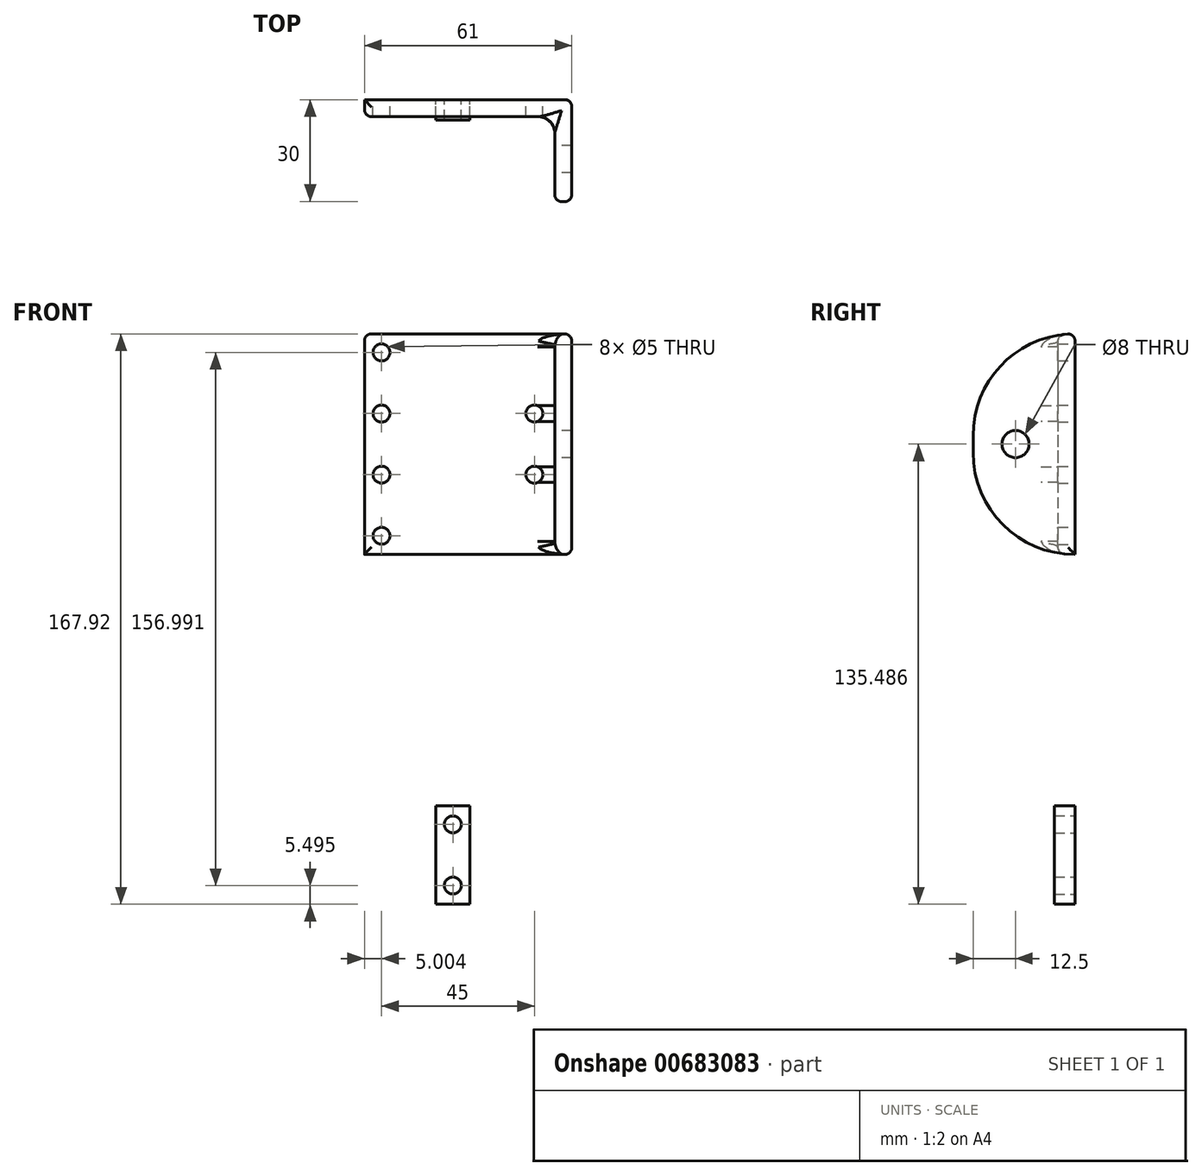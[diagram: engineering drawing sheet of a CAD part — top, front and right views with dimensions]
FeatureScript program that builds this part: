
annotation { "Feature Type Name" : "Feature", "Feature Type Description" : "" }
export const myFeature = defineFeature(function(context is Context, id is Id, definition is map)
    precondition{}
    {
        {
            var Q0;
            Q0=qCreatedBy(makeId("Front.planeOp"),FACE);
            var sketch = newSketch(context, id + "F0", { "sketchPlane" : qUnion([Q0])});
            skLineSegment(sketch, "E0.bottom", {"start": v(12.21, 1.73) * mm, "end": v(68.21, 1.73) * mm});
            skLineSegment(sketch, "E0.top", {"start": v(12.21, -63.27) * mm, "end": v(68.21, -63.27) * mm});
            skLineSegment(sketch, "E0.left", {"start": v(12.21, 1.73) * mm, "end": v(12.21, -63.27) * mm});
            skLineSegment(sketch, "E0.right", {"start": v(68.21, 1.73) * mm, "end": v(68.21, -63.27) * mm});
            skLineSegment(sketch, "E1", {"start": v(17.21, 42.37) * mm, "end": v(17.21, -87.97) * mm, "construction": true});
            skLineSegment(sketch, "E2", {"start": v(62.21, 27.17) * mm, "end": v(62.21, -88.73) * mm, "construction": true});
            skLineSegment(sketch, "E3", {"start": v(236.56, -57.77) * mm, "end": v(-18.05, -57.77) * mm, "construction": true});
            skLineSegment(sketch, "E4", {"start": v(95.96, -39.77) * mm, "end": v(-20.33, -39.77) * mm, "construction": true});
            skPoint(sketch, "E5", {"position": v(17.21, -57.77) * mm});
            skPoint(sketch, "E6", {"position": v(62.21, -39.77) * mm});
            skLineSegment(sketch, "E7.bottom", {"start": v(68.21, 1.73) * mm, "end": v(73.21, 1.73) * mm});
            skLineSegment(sketch, "E7.top", {"start": v(68.21, -63.27) * mm, "end": v(73.21, -63.27) * mm});
            skLineSegment(sketch, "E7.right", {"start": v(73.21, 1.73) * mm, "end": v(73.21, -63.27) * mm});
            skLineSegment(sketch, "E8", {"start": v(86.47, -3.77) * mm, "end": v(-13.74, -3.77) * mm, "construction": true});
            skLineSegment(sketch, "E9", {"start": v(85.33, -21.77) * mm, "end": v(-21.85, -21.77) * mm, "construction": true});
            skPoint(sketch, "E10", {"position": v(62.21, -21.77) * mm});
            skPoint(sketch, "E11", {"position": v(62.21, -3.77) * mm});
            skPoint(sketch, "E12", {"position": v(17.21, -3.77) * mm});
            skPoint(sketch, "E13", {"position": v(17.21, -21.77) * mm});
            skPoint(sketch, "E14", {"position": v(17.21, -39.77) * mm});
            skPoint(sketch, "E15", {"position": v(-24.57, -102) * mm});
            skSolve(sketch);
        }
        {
            var Q0;
            Q0=makeQuery(id+"F0.imprint","IMPRINT",FACE,{"disambiguationData":[TD([[makeQuery(id+"F0.imprint","IMPRINT",EDGE,{"derivedFrom":sQuery(id+"F0.wireOp",EDGE,"E7.bottom")}),-1.0]])]});
            extrude(context, id + "F1", {"entities" : qUnion([Q0]), "depth" : 30 * mm, "offsetDistance" : 25 * mm});
        }
        {
            var Q0;
            Q0 = qSketchRegion(id + "F0", true);
            extrude(context, id + "F2", {"entities" : qUnion([Q0]), "operationType" : NewBodyOperationType.ADD, "depth" : 5 * mm, "offsetDistance" : 25 * mm});
        }
        {
            var Q0;
            Q0=makeQuery(id+"F1.opExtrude","SWEPT_FACE",FACE,{"disambiguationData":[OSD([sQuery(id+"F0.wireOp",EDGE,"E0.right")])]});
            var sketch = newSketch(context, id + "F3", { "sketchPlane" : qUnion([Q0])});
            skPoint(sketch, "E16", {"position": v(17.5, -30.77) * mm});
            skPoint(sketch, "E16.positionSnap0", {"position": v(17.5, -63.27) * mm});
            skPoint(sketch, "E16.positionSnap1", {"position": v(30, -30.77) * mm});
            skSolve(sketch);
        }
        {
            var Q0;
            Q0=sQuery(id+"F3.wireOp",VERTEX,"E16");
            var Q1;
            Q1=makeQuery(id+"F1.opExtrude","SWEPT_BODY",BODY,{"disambiguationData":[OSD([sQuery(id+"F0.wireOp",EDGE,"E7.bottom"),sQuery(id+"F0.wireOp",EDGE,"E7.top"),sQuery(id+"F0.wireOp",EDGE,"E0.right"),sQuery(id+"F0.wireOp",EDGE,"E7.right")])]});
            hole(context, id + "F4", {"style" : HoleStyle.SIMPLE, "endStyle" : HoleEndStyle.THROUGH, "holeDiameter" : 8 * mm, "majorDiameter" : 5 * mm, "isTappedThrough" : true, "tappedDepth" : 12 * mm, "tapClearance" : 3, "locations" : qUnion([Q0]), "scope" : qUnion([Q1])});
        }
        {
            var Q0;
            Q0=makeQuery(id+"F1.opExtrude","CAP_EDGE",EDGE,{"disambiguationData":[OSD([sQuery(id+"F0.wireOp",EDGE,"E7.top")])],"isStart":false});
            var Q1;
            Q1=makeQuery(id+"F1.opExtrude","CAP_EDGE",EDGE,{"disambiguationData":[OSD([sQuery(id+"F0.wireOp",EDGE,"E7.bottom")])],"isStart":false});
            fillet(context, id + "F5", {"entities" : qUnion([Q0, Q1]), "radius" : 30 * mm, "allowEdgeOverflow" : false});
        }
        {
            var Q0;
            Q0=sQuery(id+"F0.wireOp",VERTEX,"E5");
            var Q1;
            Q1=makeQuery(id+"F1.opExtrude","SWEPT_BODY",BODY,{"disambiguationData":[OSD([sQuery(id+"F0.wireOp",EDGE,"E7.bottom"),sQuery(id+"F0.wireOp",EDGE,"E7.top"),sQuery(id+"F0.wireOp",EDGE,"E0.right"),sQuery(id+"F0.wireOp",EDGE,"E7.right")])]});
            hole(context, id + "F6", {"style" : HoleStyle.SIMPLE, "endStyle" : HoleEndStyle.THROUGH, "oppositeDirection" : true, "holeDiameter" : 5 * mm, "majorDiameter" : 5 * mm, "isTappedThrough" : true, "tappedDepth" : 12 * mm, "tapClearance" : 3, "locations" : qUnion([Q0]), "scope" : qUnion([Q1])});
        }
        {
            var Q0;
            Q0=sQuery(id+"F0.wireOp",VERTEX,"E6");
            var Q1;
            Q1=makeQuery(id+"F1.opExtrude","SWEPT_BODY",BODY,{"disambiguationData":[OSD([sQuery(id+"F0.wireOp",EDGE,"E7.bottom"),sQuery(id+"F0.wireOp",EDGE,"E7.top"),sQuery(id+"F0.wireOp",EDGE,"E0.right"),sQuery(id+"F0.wireOp",EDGE,"E7.right")])]});
            hole(context, id + "F7", {"style" : HoleStyle.SIMPLE, "endStyle" : HoleEndStyle.THROUGH, "oppositeDirection" : true, "holeDiameter" : 5 * mm, "majorDiameter" : 5 * mm, "isTappedThrough" : true, "tappedDepth" : 12 * mm, "tapClearance" : 3, "locations" : qUnion([Q0]), "scope" : qUnion([Q1])});
        }
        {
            var Q0;
            Q0=sQuery(id+"F0.wireOp",VERTEX,"E10");
            var Q1;
            Q1=sQuery(id+"F0.wireOp",VERTEX,"E13");
            var Q2;
            Q2=sQuery(id+"F0.wireOp",VERTEX,"E14");
            var Q3;
            Q3=sQuery(id+"F0.wireOp",VERTEX,"E12");
            var Q4;
            Q4=makeQuery(id+"F1.opExtrude","SWEPT_BODY",BODY,{"disambiguationData":[OSD([sQuery(id+"F0.wireOp",EDGE,"E7.bottom"),sQuery(id+"F0.wireOp",EDGE,"E7.top"),sQuery(id+"F0.wireOp",EDGE,"E0.right"),sQuery(id+"F0.wireOp",EDGE,"E7.right")])]});
            hole(context, id + "F8", {"style" : HoleStyle.SIMPLE, "endStyle" : HoleEndStyle.THROUGH, "oppositeDirection" : true, "holeDiameter" : 5 * mm, "majorDiameter" : 5 * mm, "isTappedThrough" : true, "tappedDepth" : 12 * mm, "tapClearance" : 3, "locations" : qUnion([Q0, Q1, Q2, Q3]), "scope" : qUnion([Q4])});
        }
        {
            var Q0;
            Q0=makeQuery(id+"F5.opFillet","BLEND_EDGE",EDGE,{"blendedFrom":[makeQuery(id+"F1.opExtrude","CAP_EDGE",EDGE,{"disambiguationData":[OSD([sQuery(id+"F0.wireOp",EDGE,"E7.bottom")])],"isStart":false}),makeQuery(id+"F1.opExtrude","SWEPT_FACE",FACE,{"disambiguationData":[OSD([sQuery(id+"F0.wireOp",EDGE,"E7.right")])]})],"blendedInto":[makeQuery(id+"F1.opExtrude","SWEPT_FACE",FACE,{"disambiguationData":[OSD([sQuery(id+"F0.wireOp",EDGE,"E7.right")])]})]});
            var Q1;
            Q1=makeQuery(id+"F5.opFillet","BLEND_EDGE",EDGE,{"blendedFrom":[makeQuery(id+"F1.opExtrude","CAP_EDGE",EDGE,{"disambiguationData":[OSD([sQuery(id+"F0.wireOp",EDGE,"E7.bottom")])],"isStart":false}),makeQuery(id+"F1.opExtrude","SWEPT_FACE",FACE,{"disambiguationData":[OSD([sQuery(id+"F0.wireOp",EDGE,"E0.right")])]})],"blendedInto":[makeQuery(id+"F1.opExtrude","SWEPT_FACE",FACE,{"disambiguationData":[OSD([sQuery(id+"F0.wireOp",EDGE,"E0.right")])]})]});
            var Q2;
            {var subQ0=sQuery(id+"F0.wireOp",EDGE,"E7.bottom");Q2=makeQuery(id+"F5.opFillet","BLEND_EDGE",EDGE,{"blendedFrom":[makeQuery(id+"F1.opExtrude","CAP_EDGE",EDGE,{"disambiguationData":[OSD([subQ0])],"isStart":false}),makeQuery(id+"F2.opExtrude","CAP_FACE",FACE,{"disambiguationData":[OSD([sQuery(id+"F0.wireOp",EDGE,"E0.bottom"),sQuery(id+"F0.wireOp",EDGE,"E0.top"),sQuery(id+"F0.wireOp",EDGE,"E0.left"),subQ0,sQuery(id+"F0.wireOp",EDGE,"E7.top"),sQuery(id+"F0.wireOp",EDGE,"E7.right")])],"isStart":false})],"blendedInto":[makeQuery(id+"F2.opExtrude","CAP_FACE",FACE,{"disambiguationData":[OSD([sQuery(id+"F0.wireOp",EDGE,"E0.bottom"),sQuery(id+"F0.wireOp",EDGE,"E0.top"),sQuery(id+"F0.wireOp",EDGE,"E0.left"),subQ0,sQuery(id+"F0.wireOp",EDGE,"E7.top"),sQuery(id+"F0.wireOp",EDGE,"E7.right")])],"isStart":false})]});}
            var Q3;
            Q3=makeQuery(id+"F2.opExtrude","CAP_EDGE",EDGE,{"disambiguationData":[OSD([sQuery(id+"F0.wireOp",EDGE,"E0.left")])],"isStart":false});
            var Q4;
            {var subQ0=sQuery(id+"F0.wireOp",EDGE,"E7.top");Q4=makeQuery(id+"F5.opFillet","BLEND_EDGE",EDGE,{"blendedFrom":[makeQuery(id+"F1.opExtrude","CAP_EDGE",EDGE,{"disambiguationData":[OSD([subQ0])],"isStart":false}),makeQuery(id+"F2.opExtrude","CAP_FACE",FACE,{"disambiguationData":[OSD([sQuery(id+"F0.wireOp",EDGE,"E0.bottom"),sQuery(id+"F0.wireOp",EDGE,"E0.top"),sQuery(id+"F0.wireOp",EDGE,"E0.left"),sQuery(id+"F0.wireOp",EDGE,"E7.bottom"),subQ0,sQuery(id+"F0.wireOp",EDGE,"E7.right")])],"isStart":false})],"blendedInto":[makeQuery(id+"F2.opExtrude","CAP_FACE",FACE,{"disambiguationData":[OSD([sQuery(id+"F0.wireOp",EDGE,"E0.bottom"),sQuery(id+"F0.wireOp",EDGE,"E0.top"),sQuery(id+"F0.wireOp",EDGE,"E0.left"),sQuery(id+"F0.wireOp",EDGE,"E7.bottom"),subQ0,sQuery(id+"F0.wireOp",EDGE,"E7.right")])],"isStart":false})]});}
            var Q5;
            Q5=makeQuery(id+"F5.opFillet","BLEND_FACE",FACE,{"disambiguationData":[OSD([sQuery(id+"F0.wireOp",EDGE,"E7.bottom")])]});
            var Q6;
            Q6=makeQuery(id+"F1.opExtrude","CAP_EDGE",EDGE,{"disambiguationData":[OSD([sQuery(id+"F0.wireOp",EDGE,"E7.right")])],"isStart":true});
            var Q7;
            Q7=makeQuery(id+"F5.opFillet","BLEND_EDGE",EDGE,{"blendedFrom":[makeQuery(id+"F1.opExtrude","CAP_EDGE",EDGE,{"disambiguationData":[OSD([sQuery(id+"F0.wireOp",EDGE,"E7.top")])],"isStart":false}),makeQuery(id+"F1.opExtrude","SWEPT_FACE",FACE,{"disambiguationData":[OSD([sQuery(id+"F0.wireOp",EDGE,"E0.right")])]})],"blendedInto":[makeQuery(id+"F1.opExtrude","SWEPT_FACE",FACE,{"disambiguationData":[OSD([sQuery(id+"F0.wireOp",EDGE,"E0.right")])]})]});
            var Q8;
            Q8=makeQuery(id+"F1.opExtrude","CAP_EDGE",EDGE,{"disambiguationData":[OSD([sQuery(id+"F0.wireOp",EDGE,"E0.right")])],"isStart":false});
            var Q9;
            Q9=makeQuery(id+"F1.opExtrude","CAP_EDGE",EDGE,{"disambiguationData":[OSD([sQuery(id+"F0.wireOp",EDGE,"E7.right")])],"isStart":false});
            var Q10;
            Q10=makeQuery(id+"F5.opFillet","BLEND_EDGE",EDGE,{"blendedFrom":[makeQuery(id+"F1.opExtrude","CAP_EDGE",EDGE,{"disambiguationData":[OSD([sQuery(id+"F0.wireOp",EDGE,"E7.top")])],"isStart":false}),makeQuery(id+"F1.opExtrude","SWEPT_FACE",FACE,{"disambiguationData":[OSD([sQuery(id+"F0.wireOp",EDGE,"E7.right")])]})],"blendedInto":[makeQuery(id+"F1.opExtrude","SWEPT_FACE",FACE,{"disambiguationData":[OSD([sQuery(id+"F0.wireOp",EDGE,"E7.right")])]})]});
            fillet(context, id + "F9", {"entities" : qUnion([Q0, Q1, Q2, Q3, Q4, Q5, Q6, Q7, Q8, Q9, Q10]), "radius" : 2 * mm, "tangentPropagation" : true, "allowEdgeOverflow" : false});
        }
        {
            var Q0;
            Q0=qCreatedBy(makeId("Front.planeOp"),FACE);
            var sketch = newSketch(context, id + "F10", { "sketchPlane" : qUnion([Q0])});
            skLineSegment(sketch, "E17.bottom", {"start": v(33.22, -166.26) * mm, "end": v(43.22, -166.26) * mm});
            skLineSegment(sketch, "E17.top", {"start": v(33.22, -137.26) * mm, "end": v(43.22, -137.26) * mm});
            skLineSegment(sketch, "E17.left", {"start": v(33.22, -166.26) * mm, "end": v(33.22, -137.26) * mm});
            skLineSegment(sketch, "E17.right", {"start": v(43.22, -166.26) * mm, "end": v(43.22, -137.26) * mm});
            skPoint(sketch, "E18", {"position": v(-12.27, -130.6) * mm});
            skLineSegment(sketch, "E19", {"start": v(38.22, -166.26) * mm, "end": v(38.22, -130.35) * mm, "construction": true});
            skLineSegment(sketch, "E20", {"start": v(28.67, -160.76) * mm, "end": v(56.92, -160.76) * mm, "construction": true});
            skLineSegment(sketch, "E21", {"start": v(28.19, -142.76) * mm, "end": v(67.69, -142.76) * mm, "construction": true});
            skPoint(sketch, "E22", {"position": v(38.22, -142.76) * mm});
            skPoint(sketch, "E23", {"position": v(38.22, -160.76) * mm});
            skSolve(sketch);
        }
        {
            var Q0;
            Q0=makeQuery(id+"F10.imprint","IMPRINT",FACE,{"disambiguationData":[TD([[makeQuery(id+"F10.imprint","IMPRINT",EDGE,{"derivedFrom":sQuery(id+"F10.wireOp",EDGE,"E17.bottom")}),1.0]])]});
            extrude(context, id + "F11", {"entities" : qUnion([Q0]), "depth" : 6 * mm, "offsetDistance" : 25 * mm});
        }
        {
            var Q0;
            Q0=sQuery(id+"F10.wireOp",VERTEX,"E23");
            var Q1;
            Q1=sQuery(id+"F10.wireOp",VERTEX,"E22");
            var Q2;
            Q2=makeQuery(id+"F11.opExtrude","SWEPT_BODY",BODY,{"disambiguationData":[OSD([sQuery(id+"F10.wireOp",EDGE,"E17.bottom"),sQuery(id+"F10.wireOp",EDGE,"E17.top"),sQuery(id+"F10.wireOp",EDGE,"E17.left"),sQuery(id+"F10.wireOp",EDGE,"E17.right")])]});
            hole(context, id + "F12", {"style" : HoleStyle.SIMPLE, "endStyle" : HoleEndStyle.THROUGH, "oppositeDirection" : true, "holeDiameter" : 5 * mm, "majorDiameter" : 5 * mm, "isTappedThrough" : true, "tappedDepth" : 12 * mm, "tapClearance" : 3, "locations" : qUnion([Q0, Q1]), "scope" : qUnion([Q2])});
        }
        {
            var Q0;
            Q0=makeQuery(id+"F2.boolean.opBoolean","INTERSECT",EDGE,{"derivedFrom":[makeQuery(id+"F1.opExtrude","SWEPT_FACE",FACE,{"disambiguationData":[OSD([sQuery(id+"F0.wireOp",EDGE,"E0.right")])]}),makeQuery(id+"F2.opExtrude","CAP_FACE",FACE,{"disambiguationData":[OSD([sQuery(id+"F0.wireOp",EDGE,"E0.bottom"),sQuery(id+"F0.wireOp",EDGE,"E0.top"),sQuery(id+"F0.wireOp",EDGE,"E0.left"),sQuery(id+"F0.wireOp",EDGE,"E7.bottom"),sQuery(id+"F0.wireOp",EDGE,"E7.top"),sQuery(id+"F0.wireOp",EDGE,"E7.right")])],"isStart":false})]});
            fillet(context, id + "F13", {"entities" : qUnion([Q0]), "radius" : 5 * mm, "tangentPropagation" : true, "allowEdgeOverflow" : false});
        }
    });
